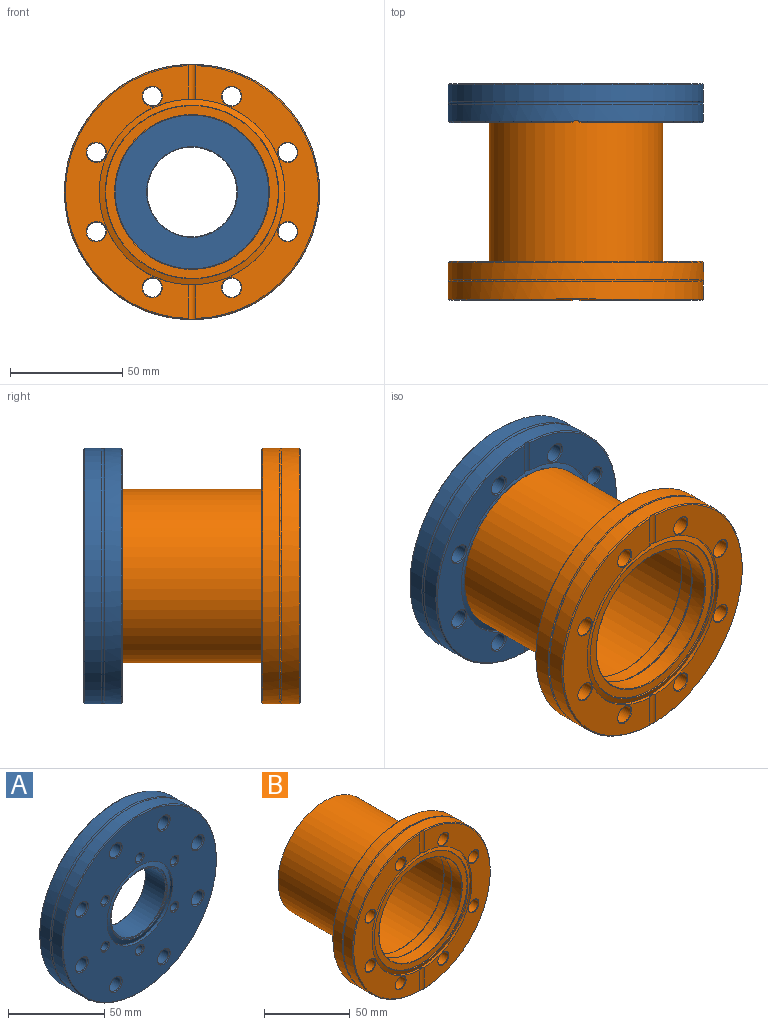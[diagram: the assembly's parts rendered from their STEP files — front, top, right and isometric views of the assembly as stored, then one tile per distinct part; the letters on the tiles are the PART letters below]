
ASSEMBLY  parts=2 mates=1
PART A: 63 faces, bbox 123x17.3x123 mm
  f0: cylinder r=2.68mm len=11.47mm, axis (0,-1,0), area 193.4mm2, adj f1,f2
  f1: cone r=3.19mm half-angle=45deg, axis (0,-1,0), area 13.3mm2, adj f0,f32
  f2: cone r=2.68mm half-angle=59deg, axis (0,-1,0), area 26.4mm2, adj f0
  f3: cone r=3.19mm half-angle=45deg, axis (0,-1,0), area 13.3mm2, adj f4,f32
  f4: cylinder r=2.68mm len=11.47mm, axis (0,-1,0), area 193.4mm2, adj f3,f6
  f5: cylinder r=2.68mm len=11.47mm, axis (0,-1,0), area 193.4mm2, adj f7,f8
  f6: cone r=2.68mm half-angle=59deg, axis (0,-1,0), area 26.4mm2, adj f4
  f7: cone r=3.19mm half-angle=45deg, axis (0,-1,0), area 13.3mm2, adj f5,f32
  f8: cone r=2.68mm half-angle=59deg, axis (0,-1,0), area 26.4mm2, adj f5
  f9: cone r=3.19mm half-angle=45deg, axis (0,-1,0), area 13.3mm2, adj f11,f32
  f10: cone r=2.68mm half-angle=59deg, axis (0,-1,0), area 26.4mm2, adj f11
  f11: cylinder r=2.68mm len=11.47mm, axis (0,-1,0), area 193.4mm2, adj f9,f10
  f12: cone r=3.19mm half-angle=45deg, axis (0,-1,0), area 13.3mm2, adj f14,f32
  f13: cone r=2.68mm half-angle=59deg, axis (0,-1,0), area 26.4mm2, adj f14
  f14: cylinder r=2.68mm len=11.47mm, axis (0,-1,0), area 193.4mm2, adj f12,f13
  f15: cone r=3.19mm half-angle=45deg, axis (0,-1,0), area 13.3mm2, adj f17,f32
  f16: cone r=2.68mm half-angle=59deg, axis (0,-1,0), area 26.4mm2, adj f17
  f17: cylinder r=2.68mm len=11.47mm, axis (0,-1,0), area 193.4mm2, adj f15,f16
  f18: torus R=20.19mm, axis (0,-1,0), area 50.2mm2, adj f25,f33
  f19: torus R=57.53mm, axis (0,1,0), area 522.3mm2, adj f28,f29
  f20: cone r=56.77mm half-angle=45deg, axis (0,1,0), area 255.1mm2, adj f29,f32
  f21: cylinder r=2.38mm len=15.52mm, axis (0,0,1), area 61.7mm2, adj f23,f24,f26,f28,f30,f31
  f22: cylinder r=2.38mm len=15.52mm, axis (0,0,-1), area 61.7mm2, adj f23,f24,f26,f28,f30,f31
  f23: cone r=56.26mm half-angle=45deg, axis (0,-1,0), area 125.5mm2, adj f21,f22,f28,f30
  f24: cone r=56.26mm half-angle=45deg, axis (0,-1,0), area 125.5mm2, adj f21,f22,f28,f31
  f25: plane 76.85x76.85mm, normal (0,1,0), area 3357mm2, adj f18,f38
  f26: cylinder r=41.27mm len=82.55mm, axis (0,1,0), area 423mm2, adj f21,f22,f30,f31,f62
  f27: cone r=4.72mm half-angle=45deg, axis (0,-1,0), area 20.2mm2, adj f32,f60
  f28: cylinder r=56.77mm len=113.54mm, axis (0,-1,0), area 2659.5mm2, adj f19,f21,f22,f23,f24
  f29: cylinder r=56.77mm len=113.54mm, axis (0,-1,0), area 2659.5mm2, adj f19,f20
  f30: plane 112.47x54.49mm, normal (0,1,0), area 1962.3mm2, adj f21,f22,f23,f26,f40,f55,f58,f61
  f31: plane 112.47x54.49mm, normal (0,1,0), area 1962.3mm2, adj f21,f22,f24,f26,f43,f46,f49,f52
  f32: plane 112.52x112.52mm, normal (0,-1,0), area 7361.9mm2, adj f1,f3,f7,f9,f12,f15,f20,f27
  f33: cylinder r=19.94mm len=39.88mm, axis (0,1,0), area 1839.3mm2, adj f18,f35
  f34: cylinder r=24.13mm len=48.26mm, axis (0,1,0), area 275.3mm2, adj f32,f36
  f35: plane 41.54x41.54mm, normal (0,-1,0), area 106.3mm2, adj f33,f37
  f36: cone r=20.96mm half-angle=70deg, axis (0,1,0), area 478.6mm2, adj f34,f37
  f37: cone r=20.77mm half-angle=20deg, axis (0,-1,0), area 70.9mm2, adj f35,f36
  f38: cone r=38.42mm half-angle=20deg, axis (0,1,0), area 130.8mm2, adj f25,f62
  f39: cylinder r=4.22mm len=16.26mm, axis (0,1,0), area 430.7mm2, adj f40,f41
  f40: cone r=4.72mm half-angle=45deg, axis (0,1,0), area 20.2mm2, adj f30,f39
  f41: cone r=4.72mm half-angle=45deg, axis (0,-1,0), area 20.2mm2, adj f32,f39
  f42: cylinder r=4.22mm len=16.26mm, axis (0,1,0), area 430.7mm2, adj f43,f44
  f43: cone r=4.72mm half-angle=45deg, axis (0,1,0), area 20.2mm2, adj f31,f42
  f44: cone r=4.72mm half-angle=45deg, axis (0,-1,0), area 20.2mm2, adj f32,f42
  f45: cylinder r=4.22mm len=16.26mm, axis (0,1,0), area 430.7mm2, adj f46,f47
  f46: cone r=4.72mm half-angle=45deg, axis (0,1,0), area 20.2mm2, adj f31,f45
  f47: cone r=4.72mm half-angle=45deg, axis (0,-1,0), area 20.2mm2, adj f32,f45
  f48: cylinder r=4.22mm len=16.26mm, axis (0,1,0), area 430.7mm2, adj f49,f50
  f49: cone r=4.72mm half-angle=45deg, axis (0,1,0), area 20.2mm2, adj f31,f48
  f50: cone r=4.72mm half-angle=45deg, axis (0,-1,0), area 20.2mm2, adj f32,f48
  f51: cylinder r=4.22mm len=16.26mm, axis (0,1,0), area 430.7mm2, adj f52,f53
  f52: cone r=4.72mm half-angle=45deg, axis (0,1,0), area 20.2mm2, adj f31,f51
  f53: cone r=4.72mm half-angle=45deg, axis (0,-1,0), area 20.2mm2, adj f32,f51
  f54: cylinder r=4.22mm len=16.26mm, axis (0,1,0), area 430.7mm2, adj f55,f56
  f55: cone r=4.72mm half-angle=45deg, axis (0,1,0), area 20.2mm2, adj f30,f54
  f56: cone r=4.72mm half-angle=45deg, axis (0,-1,0), area 20.2mm2, adj f32,f54
  f57: cylinder r=4.22mm len=16.26mm, axis (0,1,0), area 430.7mm2, adj f58,f59
  f58: cone r=4.72mm half-angle=45deg, axis (0,1,0), area 20.2mm2, adj f30,f57
  f59: cone r=4.72mm half-angle=45deg, axis (0,-1,0), area 20.2mm2, adj f32,f57
  f60: cylinder r=4.22mm len=16.26mm, axis (0,1,0), area 430.7mm2, adj f27,f61
  f61: cone r=4.72mm half-angle=45deg, axis (0,1,0), area 20.2mm2, adj f30,f60
  f62: cone r=38.61mm half-angle=70deg, axis (0,-1,0), area 712.3mm2, adj f26,f38
PART B: 50 faces, bbox 123.4x80.3x123.4 mm
  f0: cylinder r=56.77mm len=113.54mm, axis (0,-1,0), area 2742.3mm2, adj f1,f2,f5,f11,f42
  f1: cylinder r=2.38mm len=15.52mm, axis (0,0,1), area 61.5mm2, adj f0,f2,f3,f4,f5,f6
  f2: cone r=56.77mm half-angle=45deg, axis (0,1,0), area 125.5mm2, adj f0,f1,f3,f11
  f3: plane 112.47x54.49mm, normal (0,-1,0), area 1991.8mm2, adj f1,f2,f4,f11,f12,f15,f18,f21
  f4: cylinder r=41.27mm len=82.55mm, axis (0,1,0), area 423mm2, adj f1,f3,f6,f11,f44
  f5: cone r=56.77mm half-angle=45deg, axis (0,1,0), area 125.5mm2, adj f0,f1,f6,f11
  f6: plane 112.47x54.49mm, normal (0,-1,0), area 1991.8mm2, adj f1,f4,f5,f11,f24,f27,f30,f33
  f7: cylinder r=56.77mm len=113.54mm, axis (0,-1,0), area 2742.3mm2, adj f39,f42
  f8: plane 112.52x112.52mm, normal (0,1,0), area 4770.7mm2, adj f13,f16,f19,f22,f25,f28,f31,f34
  f9: cylinder r=35.05mm len=70.1mm, axis (0,1,0), area 1352mm2, adj f36,f41
  f10: cylinder r=34.16mm len=68.33mm, axis (0,-1,0), area 1695.6mm2, adj f37,f38
  f11: cylinder r=2.38mm len=15.52mm, axis (0,0,-1), area 61.5mm2, adj f0,f2,f3,f4,f5,f6
  f12: cone r=4.47mm half-angle=45deg, axis (0,-1,0), area 9.8mm2, adj f3,f14
  f13: cone r=4.22mm half-angle=45deg, axis (0,1,0), area 9.8mm2, adj f8,f14
  f14: cylinder r=4.22mm len=16.76mm, axis (0,-1,0), area 444.1mm2, adj f12,f13
  f15: cone r=4.47mm half-angle=45deg, axis (0,-1,0), area 9.8mm2, adj f3,f17
  f16: cone r=4.22mm half-angle=45deg, axis (0,1,0), area 9.8mm2, adj f8,f17
  f17: cylinder r=4.22mm len=16.76mm, axis (0,-1,0), area 444.1mm2, adj f15,f16
  f18: cone r=4.47mm half-angle=45deg, axis (0,-1,0), area 9.8mm2, adj f3,f20
  f19: cone r=4.22mm half-angle=45deg, axis (0,1,0), area 9.8mm2, adj f8,f20
  f20: cylinder r=4.22mm len=16.76mm, axis (0,-1,0), area 444.1mm2, adj f18,f19
  f21: cone r=4.47mm half-angle=45deg, axis (0,-1,0), area 9.8mm2, adj f3,f23
  f22: cone r=4.22mm half-angle=45deg, axis (0,1,0), area 9.8mm2, adj f8,f23
  f23: cylinder r=4.22mm len=16.76mm, axis (0,-1,0), area 444.1mm2, adj f21,f22
  f24: cone r=4.47mm half-angle=45deg, axis (0,-1,0), area 9.8mm2, adj f6,f26
  f25: cone r=4.22mm half-angle=45deg, axis (0,1,0), area 9.8mm2, adj f8,f26
  f26: cylinder r=4.22mm len=16.76mm, axis (0,-1,0), area 444.1mm2, adj f24,f25
  f27: cone r=4.47mm half-angle=45deg, axis (0,-1,0), area 9.8mm2, adj f6,f29
  f28: cone r=4.22mm half-angle=45deg, axis (0,1,0), area 9.8mm2, adj f8,f29
  f29: cylinder r=4.22mm len=16.76mm, axis (0,-1,0), area 444.1mm2, adj f27,f28
  f30: cone r=4.47mm half-angle=45deg, axis (0,-1,0), area 9.8mm2, adj f6,f32
  f31: cone r=4.22mm half-angle=45deg, axis (0,1,0), area 9.8mm2, adj f8,f32
  f32: cylinder r=4.22mm len=16.76mm, axis (0,-1,0), area 444.1mm2, adj f30,f31
  f33: cone r=4.47mm half-angle=45deg, axis (0,-1,0), area 9.8mm2, adj f6,f35
  f34: cone r=4.22mm half-angle=45deg, axis (0,1,0), area 9.8mm2, adj f8,f35
  f35: cylinder r=4.22mm len=16.76mm, axis (0,-1,0), area 444.1mm2, adj f33,f34
  f36: torus R=35.56mm, axis (0,1,0), area 176.7mm2, adj f9,f47
  f37: torus R=34.37mm, axis (0,-1,0), area 68.7mm2, adj f10,f46
  f38: torus R=34.42mm, axis (0,1,0), area 85.9mm2, adj f10,f45
  f39: cone r=56.26mm half-angle=45deg, axis (0,-1,0), area 255.1mm2, adj f7,f8
  f40: torus R=35.05mm, axis (0,-1,0), area 180.1mm2, adj f41,f46
  f41: cone r=35.05mm half-angle=32deg, axis (0,-1,0), area 134.9mm2, adj f9,f40
  f42: torus R=57.02mm, axis (0,-1,0), area 378.4mm2, adj f0,f7
  f43: cone r=38.61mm half-angle=20deg, axis (0,-1,0), area 130.8mm2, adj f44,f45
  f44: cone r=41.27mm half-angle=70deg, axis (0,1,0), area 712.3mm2, adj f4,f43
  f45: plane 76.85x76.85mm, normal (0,-1,0), area 916.7mm2, adj f38,f43
  f46: plane 70.1x70.1mm, normal (0,1,0), area 149.6mm2, adj f37,f40
  f47: cylinder r=35.56mm len=71.12mm, axis (0,-1,0), area 14076.1mm2, adj f36,f49
  f48: cylinder r=38.56mm len=77.12mm, axis (0,-1,0), area 15263.6mm2, adj f8,f49
  f49: plane 77.12x77.12mm, normal (0,1,0), area 698.6mm2, adj f47,f48
PLACE A rot(axis=(1,0,0),180deg) t=(0,79.1,0)mm
PLACE B at identity
MATE fastened A.f20 <-> B.f48  axis (0,-1,0) through (0,71.64,0)mm
